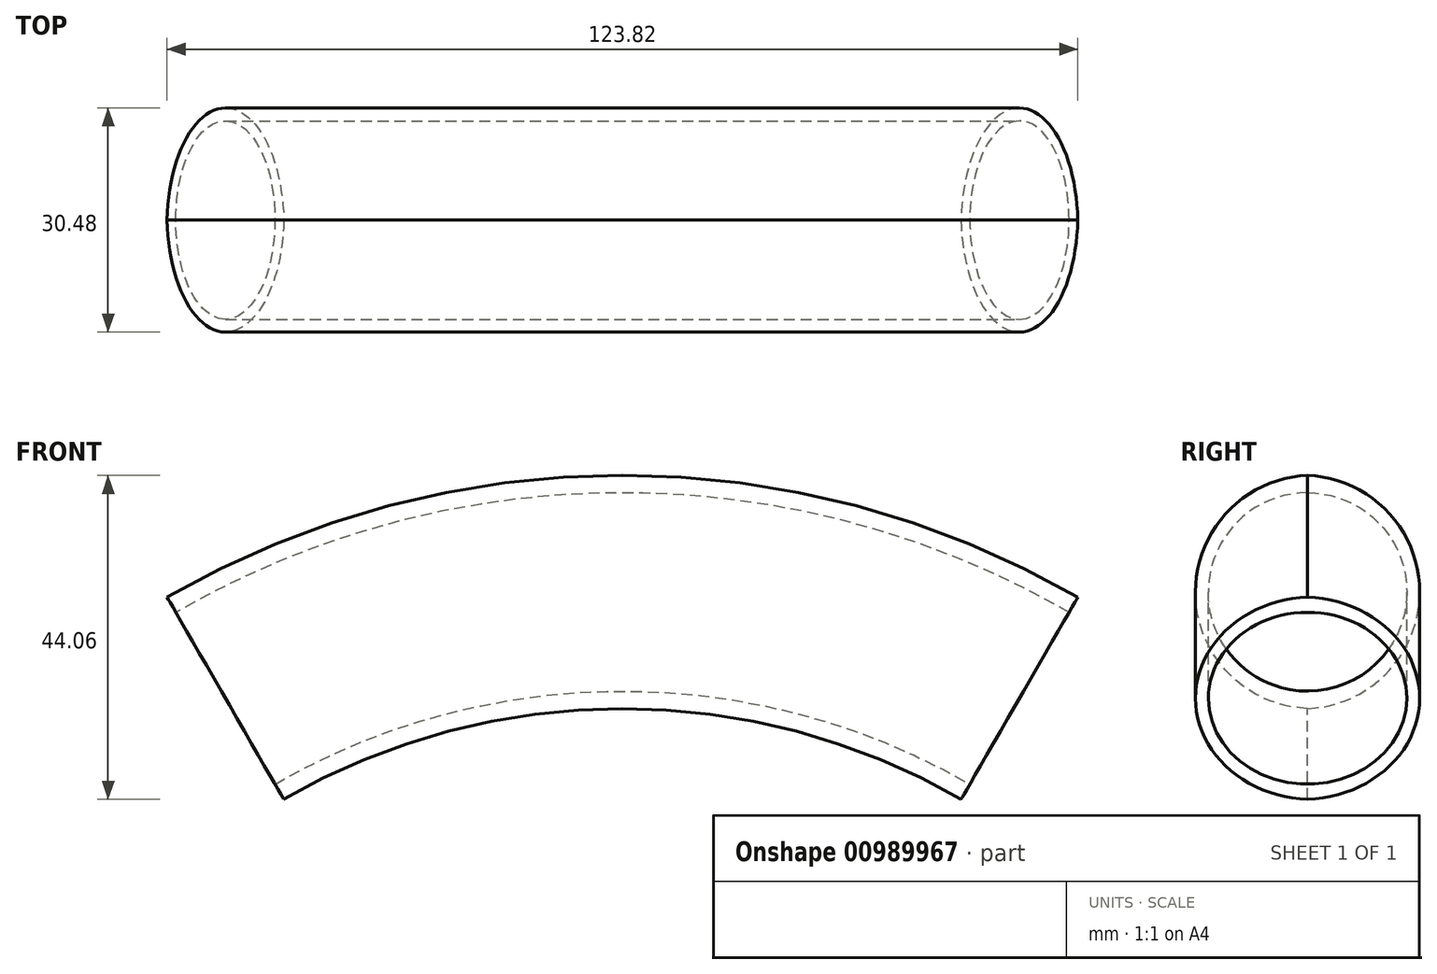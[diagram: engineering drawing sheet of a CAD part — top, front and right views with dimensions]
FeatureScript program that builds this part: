
annotation { "Feature Type Name" : "Feature", "Feature Type Description" : "" }
export const myFeature = defineFeature(function(context is Context, id is Id, definition is map)
    precondition{}
    {
        {
            var Q0;
            Q0=qCreatedBy(makeId("Front.planeOp"),FACE);
            var sketch = newSketch(context, id + "F0", { "sketchPlane" : qUnion([Q0])});
            skCircle(sketch, "E0", {"center": v(0, 0) * mm, "radius": 123.83 * mm});
            skCircle(sketch, "E1", {"center": v(0, 0) * mm, "radius": 92.08 * mm});
            skLineSegment(sketch, "E2", {"start": v(0, 0) * mm, "end": v(-61.91, 107.24) * mm});
            skLineSegment(sketch, "E3", {"start": v(0, 0) * mm, "end": v(0, 123.83) * mm, "construction": true});
            skLineSegment(sketch, "E4.MirrorCS", {"start": v(0, 0) * mm, "end": v(61.91, 107.24) * mm});
            skCircle(sketch, "E5", {"center": v(0, 0) * mm, "radius": 107.95 * mm});
            skSolve(sketch);
        }
        {
            var Q0;
            {var subQ0=sQuery(id+"F0.wireOp",EDGE,"E2");var subQ1=sQuery(id+"F0.wireOp",EDGE,"E1");var subQ2=makeQuery(id+"F0.imprint","INTERSECT",VERTEX,{"derivedFrom":[subQ1,subQ0]});Q0=makeQuery(id+"F0.imprint","IMPRINT",FACE,{"disambiguationData":[TD([[makeQuery(id+"F0.imprint","IMPRINT",EDGE,{"disambiguationData":[TD([[subQ2,1.0]])],"derivedFrom":subQ1}),-1.0]])]});}
            var Q1;
            {var subQ0=sQuery(id+"F0.wireOp",EDGE,"E2");var subQ1=sQuery(id+"F0.wireOp",EDGE,"E0");var subQ2=makeQuery(id+"F0.imprint","INTERSECT",VERTEX,{"derivedFrom":[subQ1,subQ0]});Q1=makeQuery(id+"F0.imprint","IMPRINT",FACE,{"disambiguationData":[TD([[makeQuery(id+"F0.imprint","IMPRINT",EDGE,{"disambiguationData":[TD([[subQ2,1.0]])],"derivedFrom":subQ1}),1.0]])]});}
            extrude(context, id + "F1", {"entities" : qUnion([Q0, Q1]), "depth" : 30.48 * mm, "offsetDistance" : 25.4 * mm});
        }
        {
            var Q0;
            Q0=makeQuery(id+"F1.opExtrude","SWEPT_FACE",FACE,{"disambiguationData":[OSD([sQuery(id+"F0.wireOp",EDGE,"E4.MirrorCS")])]});
            var sketch = newSketch(context, id + "F2", { "sketchPlane" : qUnion([Q0])});
            skCircle(sketch, "E6", {"center": v(-15.24, 107.95) * mm, "radius": 13.5 * mm});
            skPoint(sketch, "E6.centerSnap0", {"position": v(-30.48, 107.95) * mm});
            skPoint(sketch, "E6.centerSnap1", {"position": v(-15.24, 123.83) * mm});
            skSolve(sketch);
        }
        {
            var Q0;
            {var subQ0=sQuery(id+"F2.wireOp",EDGE,"E6");var subQ1=sQuery(id+"F0.wireOp",EDGE,"E4.MirrorCS");var subQ2=makeQuery(id+"F2.imprint","INTERSECT",VERTEX,{"derivedFrom":[makeQuery(id+"F1.opExtrude","SWEPT_EDGE",EDGE,{"disambiguationData":[OSD([sQuery(id+"F0.wireOp",EDGE,"E0"),subQ1])]}),subQ0]});Q0=makeQuery(id+"F2.imprint","IMPRINT",FACE,{"disambiguationData":[TD([[makeQuery(id+"F2.imprint","IMPRINT",EDGE,{"disambiguationData":[TD([[subQ2,-1.0]])],"derivedFrom":subQ0}),1.0]])]});}
            var Q1;
            Q1=sQuery(id+"F0.wireOp",EDGE,"E5");
            sweep(context, id + "F3", {"operationType" : NewBodyOperationType.REMOVE, "profiles" : qUnion([Q0]), "path" : qUnion([Q1])});
        }
        {
            var Q0;
            Q0=makeQuery(id+"F1.opExtrude","CAP_EDGE",EDGE,{"disambiguationData":[OSD([sQuery(id+"F0.wireOp",EDGE,"E0")])],"isStart":true});
            var Q1;
            Q1=makeQuery(id+"F1.opExtrude","CAP_EDGE",EDGE,{"disambiguationData":[OSD([sQuery(id+"F0.wireOp",EDGE,"E1")])],"isStart":true});
            var Q2;
            Q2=makeQuery(id+"F1.opExtrude","CAP_EDGE",EDGE,{"disambiguationData":[OSD([sQuery(id+"F0.wireOp",EDGE,"E0")])],"isStart":false});
            var Q3;
            Q3=makeQuery(id+"F1.opExtrude","CAP_EDGE",EDGE,{"disambiguationData":[OSD([sQuery(id+"F0.wireOp",EDGE,"E1")])],"isStart":false});
            fillet(context, id + "F4", {"entities" : qUnion([Q0, Q1, Q2, Q3]), "radius" : 15.88 * mm, "tangentPropagation" : true, "allowEdgeOverflow" : false});
        }
    });
